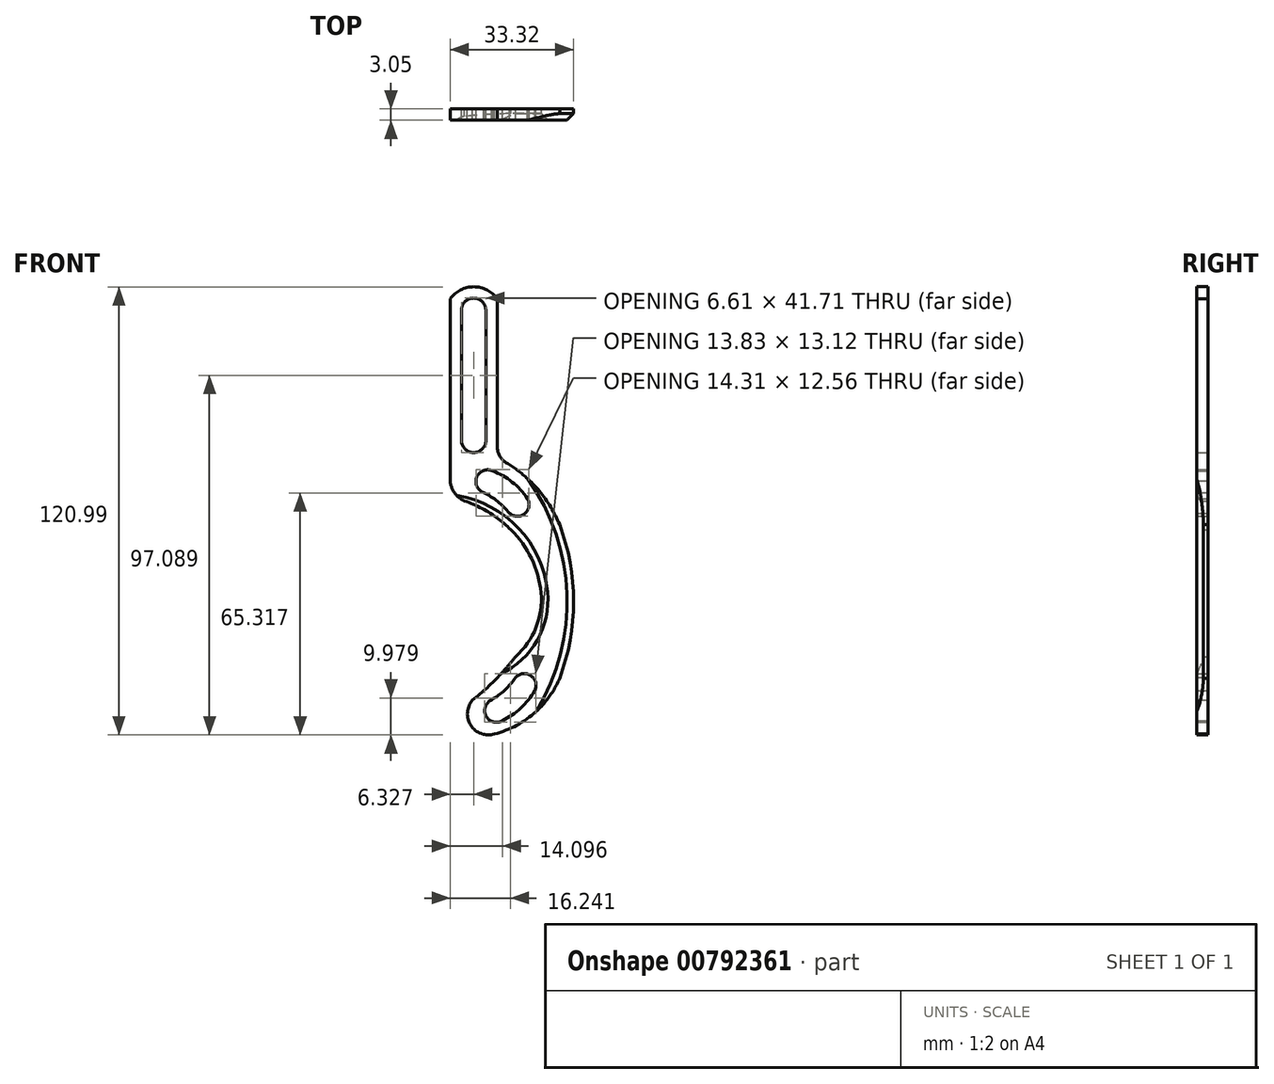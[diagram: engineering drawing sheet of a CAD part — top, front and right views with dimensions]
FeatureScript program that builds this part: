
annotation { "Feature Type Name" : "Feature", "Feature Type Description" : "" }
export const myFeature = defineFeature(function(context is Context, id is Id, definition is map)
    precondition{}
    {
        {
            var Q0;
            Q0=qCreatedBy(makeId("Front.planeOp"),FACE);
            var sketch = newSketch(context, id + "F0", { "sketchPlane" : qUnion([Q0])});
            skPoint(sketch, "E0", {"position": v(25.17, 33.8) * mm});
            skPoint(sketch, "E1", {"position": v(27.31, -22.07) * mm});
            skLineSegment(sketch, "E2", {"start": v(21.02, 28.47) * mm, "end": v(19.97, 27.1) * mm});
            skLineSegment(sketch, "E3", {"start": v(16.07, -9.67) * mm, "end": v(2.8, 4.97) * mm});
            skArc(sketch, "E4", {"start": v(21.97, -22.34) * mm, "mid": v(20.5, -26.68) * mm, "end": v(24.9, -27.97) * mm});
            skArc(sketch, "E5", {"start": v(33.67, -19.82) * mm, "mid": v(32.61, -15.78) * mm, "end": v(28.47, -16.28) * mm});
            skArc(sketch, "E6", {"start": v(22.28, 39.51) * mm, "mid": v(18.02, 37.86) * mm, "end": v(19.83, 33.66) * mm});
            skArc(sketch, "E7", {"start": v(26.85, 28.05) * mm, "mid": v(30.98, 27.97) * mm, "end": v(31.68, 32.04) * mm});
            skArc(sketch, "E8", {"start": v(26.85, 28.05) * mm, "mid": v(23.45, 31.4) * mm, "end": v(19.36, 33.88) * mm});
            skArc(sketch, "E9", {"start": v(31.68, 32.04) * mm, "mid": v(27.55, 36.49) * mm, "end": v(22.28, 39.51) * mm});
            skArc(sketch, "E10", {"start": v(24.9, -27.97) * mm, "mid": v(29.9, -24.55) * mm, "end": v(33.67, -19.82) * mm});
            skArc(sketch, "E11", {"start": v(21.53, -22.6) * mm, "mid": v(25.37, -19.84) * mm, "end": v(28.47, -16.28) * mm});
            skPoint(sketch, "E12", {"position": v(20.64, -26.9) * mm});
            skArc(sketch, "E13", {"start": v(40.38, -16.52) * mm, "mid": v(44.15, 4.22) * mm, "end": v(40.38, 24.97) * mm});
            skArc(sketch, "E14", {"start": v(22.78, -31.55) * mm, "mid": v(33.33, -26.1) * mm, "end": v(40.38, -16.52) * mm});
            skArc(sketch, "E15", {"start": v(16.85, -22.42) * mm, "mid": v(16.4, -29.2) * mm, "end": v(22.78, -31.55) * mm});
            skArc(sketch, "E16", {"start": v(16.85, -22.42) * mm, "mid": v(23.03, -16.88) * mm, "end": v(28.47, -10.62) * mm});
            skArc(sketch, "E17", {"start": v(28.47, -10.62) * mm, "mid": v(34, -2.83) * mm, "end": v(35.34, 6.62) * mm});
            skArc(sketch, "E18.trimOffspring", {"start": v(19.97, 27.1) * mm, "mid": v(19.87, 27.14) * mm, "end": v(19.77, 27.18) * mm});
            skArc(sketch, "E19", {"start": v(35.34, 6.62) * mm, "mid": v(32.78, 15.82) * mm, "end": v(27.23, 23.59) * mm});
            skLineSegment(sketch, "E20.trimOffspring", {"start": v(14.9, 20.58) * mm, "end": v(2.8, 4.97) * mm});
            skArc(sketch, "E21", {"start": v(40.38, 24.97) * mm, "mid": v(33.6, 35.54) * mm, "end": v(23.53, 43.04) * mm});
            skLineSegment(sketch, "E22", {"start": v(23.53, 43.04) * mm, "end": v(23.53, 85.96) * mm});
            skLineSegment(sketch, "E23", {"start": v(10.83, 76.07) * mm, "end": v(10.83, 36.76) * mm});
            skArc(sketch, "E24", {"start": v(27.23, 23.59) * mm, "mid": v(21.4, 28.22) * mm, "end": v(14.65, 31.4) * mm});
            skArc(sketch, "E25", {"start": v(10.83, 36.76) * mm, "mid": v(12, 33.55) * mm, "end": v(14.65, 31.4) * mm});
            skArc(sketch, "E26", {"start": v(13.86, 47.74) * mm, "mid": v(17.16, 44.44) * mm, "end": v(20.46, 47.74) * mm});
            skLineSegment(sketch, "E27", {"start": v(13.86, 74.54) * mm, "end": v(13.86, 47.74) * mm});
            skLineSegment(sketch, "E28", {"start": v(20.46, 74.54) * mm, "end": v(20.46, 47.74) * mm});
            skPoint(sketch, "E29.start.orphan", {"position": v(33.8, 47.74) * mm});
            skLineSegment(sketch, "E30", {"start": v(10.83, 76.07) * mm, "end": v(10.83, 85.96) * mm});
            skPoint(sketch, "E31.orphan", {"position": v(4.1, 88.76) * mm});
            skPoint(sketch, "E32.center.orphan", {"position": v(17.16, 74.54) * mm});
            skArc(sketch, "E33", {"start": v(23.53, 85.96) * mm, "mid": v(17.18, 89.2) * mm, "end": v(10.83, 85.96) * mm});
            skPoint(sketch, "E34.orphan", {"position": v(10.83, 88.76) * mm});
            skArc(sketch, "E35", {"start": v(20.46, 82.85) * mm, "mid": v(17.15, 86.15) * mm, "end": v(13.85, 82.85) * mm});
            skLineSegment(sketch, "E36", {"start": v(13.85, 82.85) * mm, "end": v(13.86, 74.54) * mm});
            skLineSegment(sketch, "E37", {"start": v(20.46, 82.85) * mm, "end": v(20.46, 74.54) * mm});
            skSolve(sketch);
        }
        {
            var Q0;
            Q0 = qSketchRegion(id + "F0", true);
            extrude(context, id + "F1", {"entities" : qUnion([Q0]), "depth" : 3.05 * mm, "offsetDistance" : 25.4 * mm});
        }
        {
            var Q0;
            Q0=makeQuery(id+"F1.opExtrude","SWEPT_EDGE",EDGE,{"disambiguationData":[OSD([sQuery(id+"F0.wireOp",EDGE,"E21"),sQuery(id+"F0.wireOp",EDGE,"E22")])]});
            var Q1;
            Q1=makeQuery(id+"F1.opExtrude","SWEPT_EDGE",EDGE,{"disambiguationData":[OSD([sQuery(id+"F0.wireOp",EDGE,"pL1YJwqF-fB7k-j4tk-SJGk-ljeSLr8LtVGG"),sQuery(id+"F0.wireOp",EDGE,"k8wneLHp-daPF-XCrC-Ba0j-sVALj31FYHPs")])]});
            fillet(context, id + "F2", {"entities" : qUnion([Q0, Q1]), "radius" : 5.08 * mm, "tangentPropagation" : true, "allowEdgeOverflow" : false});
        }
        {
            var Q0;
            Q0=makeQuery(id+"F1.opExtrude","CAP_EDGE",EDGE,{"disambiguationData":[OSD([sQuery(id+"F0.wireOp",EDGE,"E19")])],"isStart":false});
            var Q1;
            Q1=makeQuery(id+"F1.opExtrude","CAP_EDGE",EDGE,{"disambiguationData":[OSD([sQuery(id+"F0.wireOp",EDGE,"E17")])],"isStart":false});
            var Q2;
            Q2=makeQuery(id+"F1.opExtrude","CAP_EDGE",EDGE,{"disambiguationData":[OSD([sQuery(id+"F0.wireOp",EDGE,"E13")])],"isStart":false});
            chamfer(context, id + "F3", {"entities" : qUnion([Q0, Q1, Q2]), "width" : 1.78 * mm, "tangentPropagation" : true});
        }
    });
